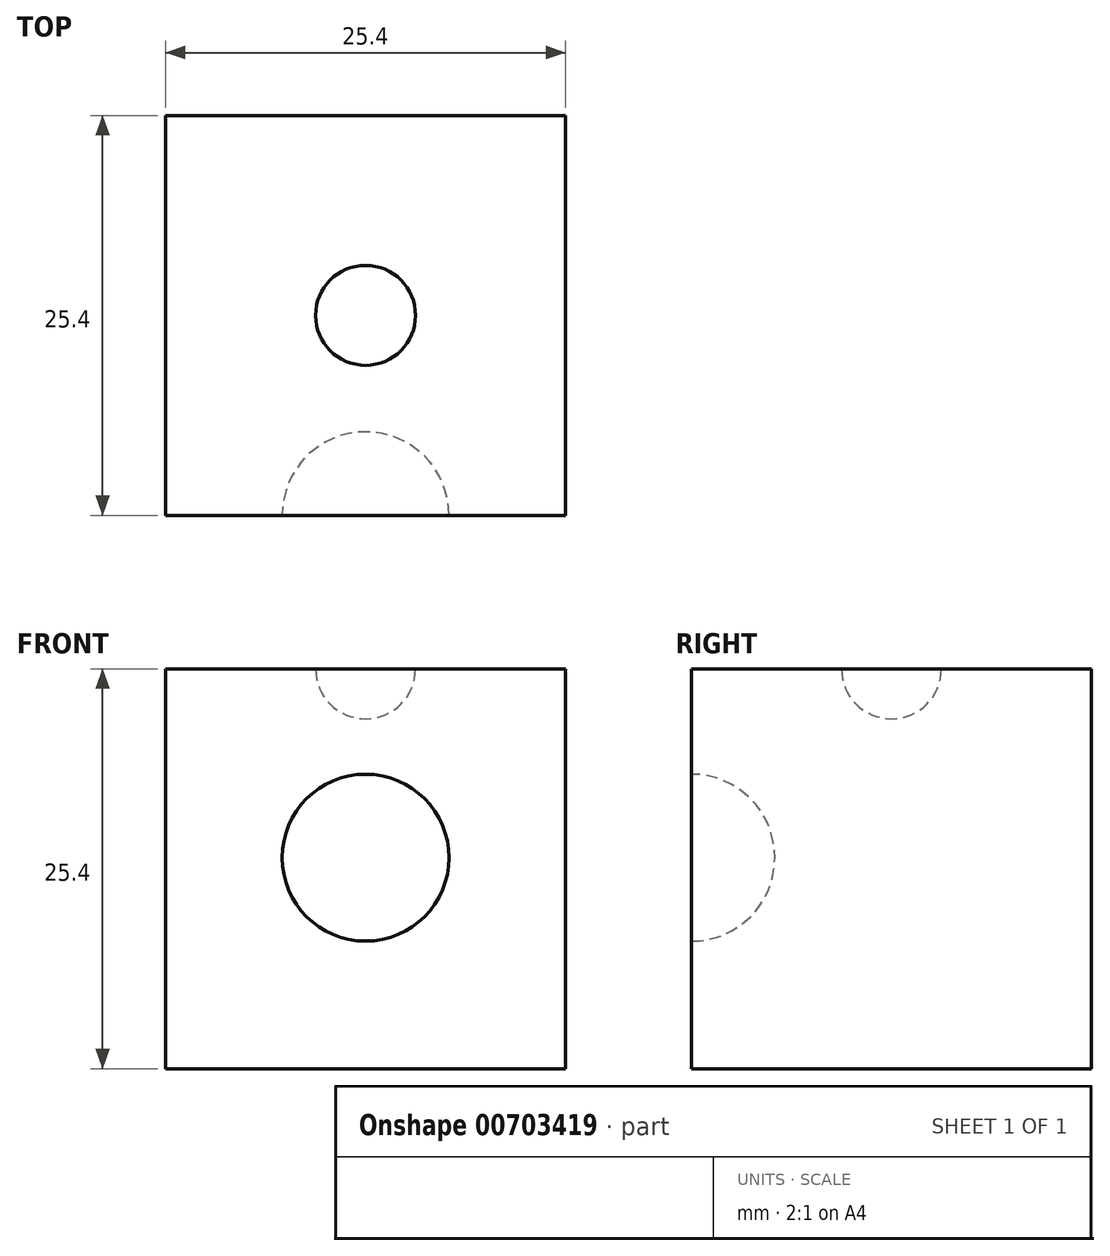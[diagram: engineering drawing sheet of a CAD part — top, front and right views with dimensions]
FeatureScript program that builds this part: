
annotation { "Feature Type Name" : "Feature", "Feature Type Description" : "" }
export const myFeature = defineFeature(function(context is Context, id is Id, definition is map)
    precondition{}
    {
        {
            var Q0;
            Q0=qCreatedBy(makeId("Top.planeOp"),FACE);
            var sketch = newSketch(context, id + "F0", { "sketchPlane" : qUnion([Q0])});
            skLineSegment(sketch, "E0.bottom", {"start": v(12.7, 12.7) * mm, "end": v(-12.7, 12.7) * mm});
            skLineSegment(sketch, "E0.top", {"start": v(12.7, -12.7) * mm, "end": v(-12.7, -12.7) * mm});
            skLineSegment(sketch, "E0.left", {"start": v(12.7, 12.7) * mm, "end": v(12.7, -12.7) * mm});
            skLineSegment(sketch, "E0.right", {"start": v(-12.7, 12.7) * mm, "end": v(-12.7, -12.7) * mm});
            skPoint(sketch, "E0.middle", {"position": v(0, 0) * mm});
            skSolve(sketch);
        }
        {
            var Q0;
            Q0 = qSketchRegion(id + "F0", true);
            extrude(context, id + "F1", {"entities" : qUnion([Q0]), "depth" : 25.4 * mm, "offsetDistance" : 25.4 * mm});
        }
        {
            var Q0;
            Q0=makeQuery(id+"F1.opExtrude","CAP_FACE",FACE,{"disambiguationData":[OSD([sQuery(id+"F0.wireOp",EDGE,"E0.bottom"),sQuery(id+"F0.wireOp",EDGE,"E0.top"),sQuery(id+"F0.wireOp",EDGE,"E0.left"),sQuery(id+"F0.wireOp",EDGE,"E0.right")])],"isStart":false});
            var sketch = newSketch(context, id + "F2", { "sketchPlane" : qUnion([Q0])});
            skCircle(sketch, "E1", {"center": v(0, 0) * mm, "radius": 3.17 * mm});
            skLineSegment(sketch, "E2", {"start": v(0, -3.17) * mm, "end": v(0, 3.17) * mm});
            skSolve(sketch);
        }
        {
            var Q0;
            {var subQ0=sQuery(id+"F2.wireOp",EDGE,"E2");Q0=makeQuery(id+"F2.imprint","IMPRINT",FACE,{"disambiguationData":[TD([[makeQuery(id+"F2.imprint","IMPRINT",EDGE,{"derivedFrom":subQ0}),-1.0]])]});}
            var Q1;
            Q1=sQuery(id+"F2.wireOp",EDGE,"E2");
            revolve(context, id + "F3", {"operationType" : NewBodyOperationType.REMOVE, "surfaceOperationType" : NewSurfaceOperationType.NEW, "entities" : qUnion([Q0]), "axis" : qUnion([Q1]), "revolveType" : RevolveType.FULL, "oppositeDirection" : true});
        }
        {
            var Q0;
            Q0=makeQuery(id+"F1.opExtrude","SWEPT_FACE",FACE,{"disambiguationData":[OSD([sQuery(id+"F0.wireOp",EDGE,"E0.top")])]});
            var sketch = newSketch(context, id + "F4", { "sketchPlane" : qUnion([Q0])});
            skCircle(sketch, "E3", {"center": v(0, 13.4) * mm, "radius": 5.3 * mm});
            skLineSegment(sketch, "E4", {"start": v(0, 18.7) * mm, "end": v(0, 8.1) * mm});
            skSolve(sketch);
        }
        {
            var Q0;
            {var subQ0=sQuery(id+"F4.wireOp",EDGE,"E4");Q0=makeQuery(id+"F4.imprint","IMPRINT",FACE,{"disambiguationData":[TD([[makeQuery(id+"F4.imprint","IMPRINT",EDGE,{"derivedFrom":subQ0}),1.0]])]});}
            var Q1;
            Q1=sQuery(id+"F4.wireOp",EDGE,"E4");
            revolve(context, id + "F5", {"operationType" : NewBodyOperationType.REMOVE, "surfaceOperationType" : NewSurfaceOperationType.NEW, "entities" : qUnion([Q0]), "axis" : qUnion([Q1]), "revolveType" : RevolveType.FULL, "oppositeDirection" : true});
        }
    });
